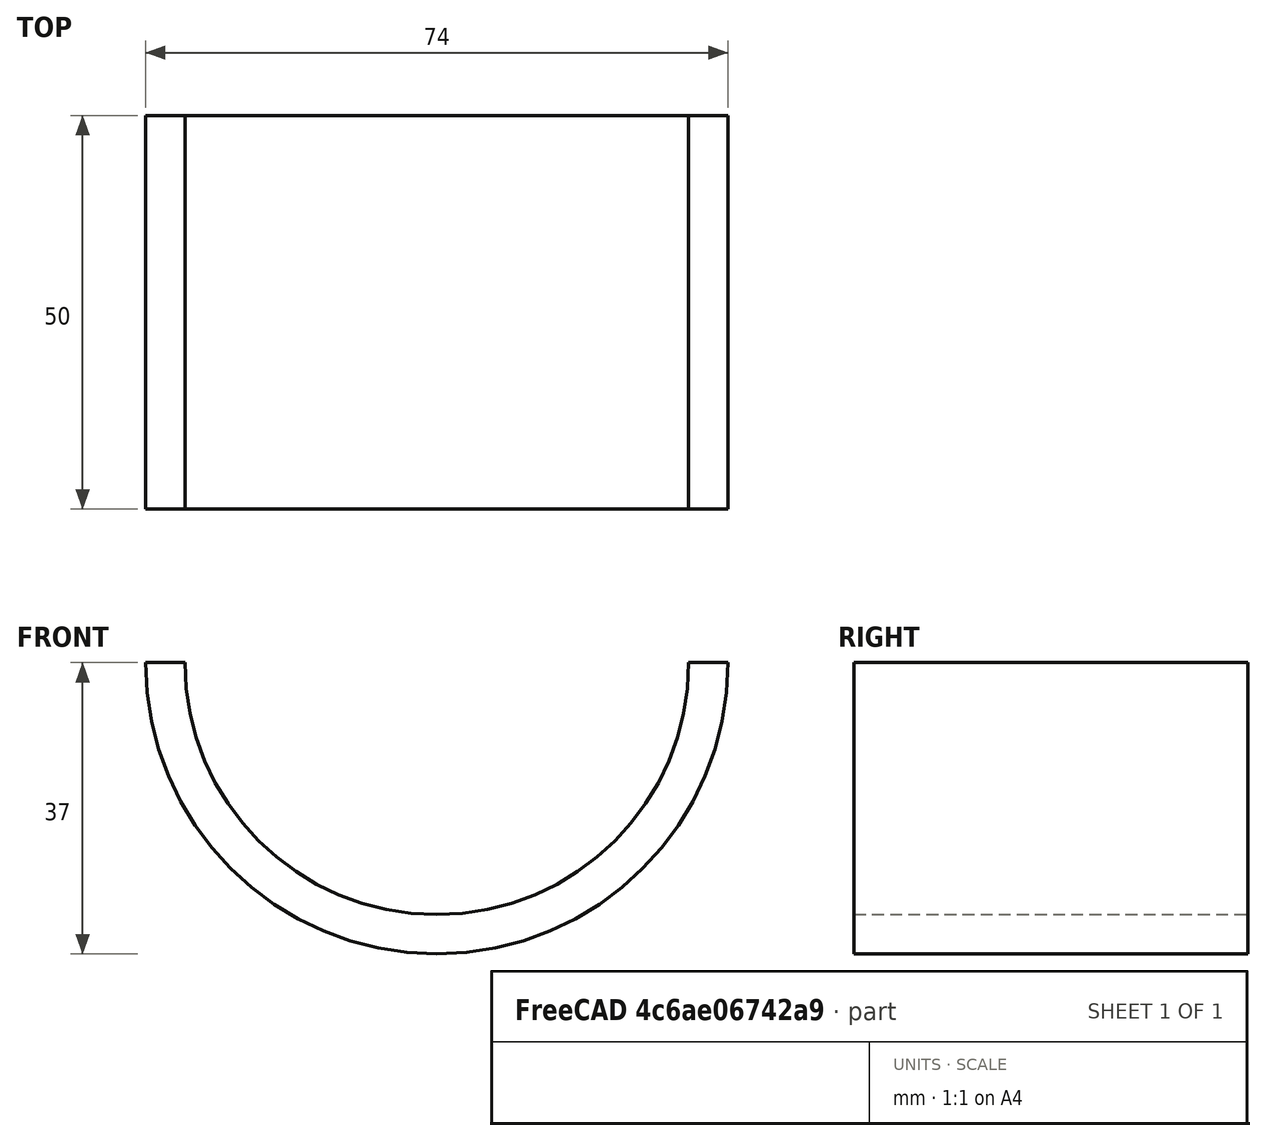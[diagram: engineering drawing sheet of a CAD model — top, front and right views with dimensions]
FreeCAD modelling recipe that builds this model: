
FCSTD DOCUMENT  (FreeCAD 1.0R38806 (Git))
Label: curved2
License: All rights reserved
LicenseURL: https://en.wikipedia.org/wiki/All_rights_reserved
objects: Sketcher::SketchObject×1, PartDesign::Pad×1, PartDesign::Body×1
note: 6 computed .brp shape members not serialized (recipe doc carries the construction recipe); baked Part::Feature solids carry a one-line shape summary decoded from their .brp

FEATURE [Sketcher::SketchObject] Sketch
  ArcFitTolerance = 1e-06
  AttachmentSupport = -> [XZ_Plane]
  FullyConstrained = true
  MakeInternals = false
  MapMode = 5
  Placement = pos=(0,0,0) rot=(1,0,0;1.5708rad)
  sketch-geometry (4):
    g0: ArcOfCircle CenterX=0 CenterY=0 CenterZ=0 NormalX=0 NormalY=0 NormalZ=1 AngleXU=0 Radius=37 StartAngle=3.14159 EndAngle=6.28319
    g1: ArcOfCircle CenterX=0 CenterY=0 CenterZ=0 NormalX=0 NormalY=0 NormalZ=1 AngleXU=0 Radius=32 StartAngle=3.14159 EndAngle=6.28319
    g2: LineSegment StartX=-37 StartY=0 StartZ=0 EndX=-32 EndY=3.9e-15 EndZ=0
    g3: LineSegment StartX=32 StartY=-7.8e-15 StartZ=0 EndX=37 EndY=-9.1e-15 EndZ=0
  constraints (12):
    c: Coincident(g0,g-1)
    c: PointOnObject(g0,g-1)
    c: PointOnObject(g0,g-1)
    c: Radius(g0) = 37
    c: Coincident(g1,g0)
    c: PointOnObject(g1,g-1)
    c: PointOnObject(g1,g-1)
    c: Distance(g1,g0) = 5
    c: Coincident(g2,g0)
    c: Coincident(g2,g1)
    c: Coincident(g3,g1)
    c: Coincident(g3,g0)
FEATURE [PartDesign::Pad] Pad
  Direction = (0,-1,2e-16)
  Length = 50
  Length2 = 10
  Placement = pos=(0,0,0) rot=(1,0,0;1.5708rad)
  Profile = -> Sketch
  ReferenceAxis = -> Sketch [N_Axis]
  Refine = true
  Suppressed = false
  Type = 0
FEATURE [PartDesign::Body] Body
  AllowCompound = false
  Group = -> [Sketch,Pad]
  Origin = -> Origin
  Tip = -> Pad
